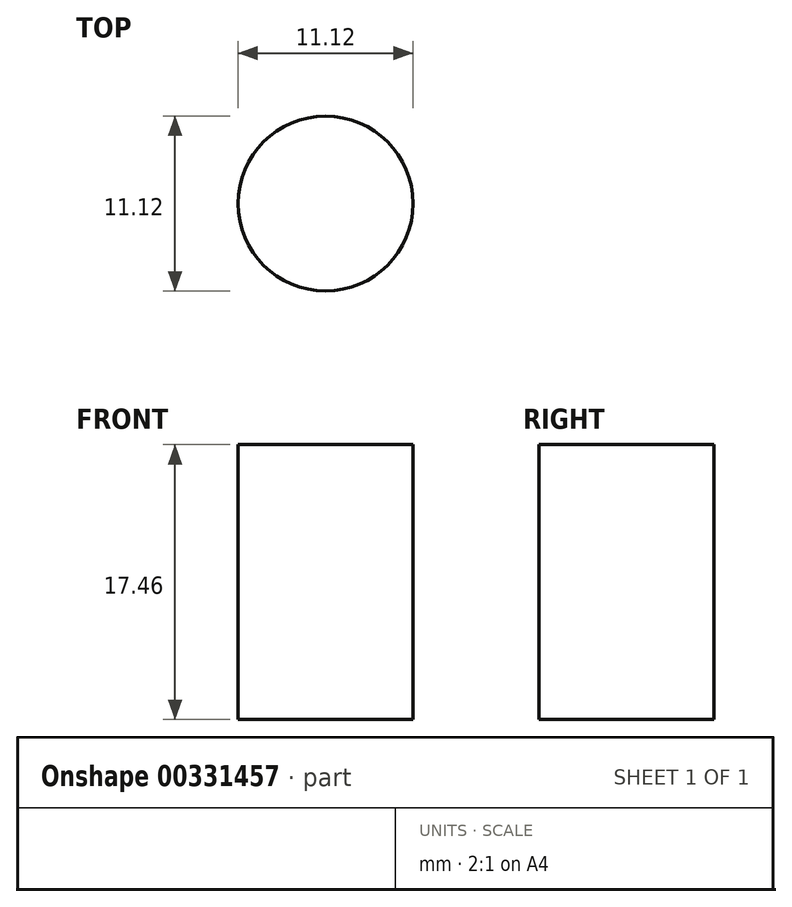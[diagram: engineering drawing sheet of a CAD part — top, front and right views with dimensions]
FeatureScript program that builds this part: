
annotation { "Feature Type Name" : "Feature", "Feature Type Description" : "" }
export const myFeature = defineFeature(function(context is Context, id is Id, definition is map)
    precondition{}
    {
        {
            var Q0;
            Q0 = qSketchRegion(id + "FxdFnskXL3LPoby_0", true);
            var sketch = newSketch(context, id + "F0", { "sketchPlane" : qUnion([Q0])});
            skSolve(sketch);
        }
        {
            var Q0;
            Q0=qCreatedBy(makeId("Top.planeOp"),FACE);
            var sketch = newSketch(context, id + "F1", { "sketchPlane" : qUnion([Q0])});
            skCircle(sketch, "E0", {"center": v(0, 0) * mm, "radius": 5.56 * mm});
            skSolve(sketch);
        }
        {
            var Q0;
            Q0 = qSketchRegion(id + "F1", true);
            var sketch = newSketch(context, id + "F2", { "sketchPlane" : qUnion([Q0])});
            skSolve(sketch);
        }
        {
            var Q0;
            Q0=makeQuery(id+"F2.imprint","IMPRINT",FACE,{"disambiguationData":[TD([[makeQuery(id+"F2.imprint","IMPRINT",EDGE,{"derivedFrom":makeQuery(id+"F1.imprint","IMPRINT",EDGE,{"derivedFrom":sQuery(id+"F1.wireOp",EDGE,"E0")})}),1.0]])]});
            extrude(context, id + "F3", {"entities" : qUnion([Q0]), "depth" : 17.46 * mm});
        }
    });
